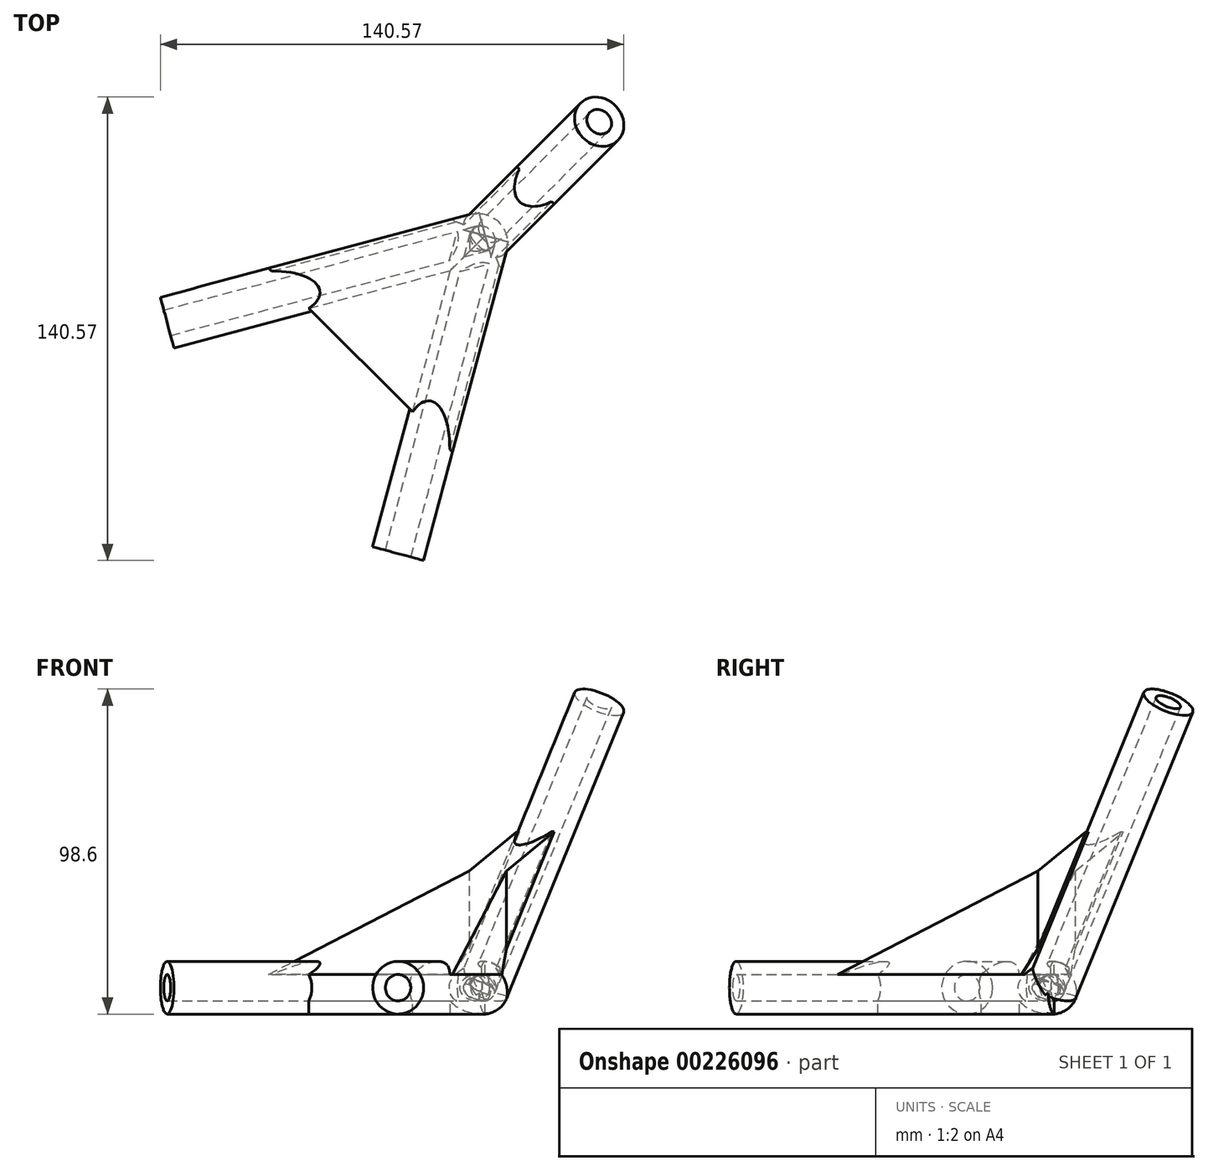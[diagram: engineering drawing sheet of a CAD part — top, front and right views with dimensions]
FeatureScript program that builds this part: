
annotation { "Feature Type Name" : "Feature", "Feature Type Description" : "" }
export const myFeature = defineFeature(function(context is Context, id is Id, definition is map)
    precondition{}
    {
        {
            var Q0;
            Q0=qCreatedBy(makeId("Right.planeOp"),FACE);
            var Q1;
            Q1=qCreatedBy(makeId("Front.planeOp"),FACE);
            cPlane(context, id + "F0", {"entities" : qUnion([Q0, Q1]), "cplaneType" : CPlaneType.MID_PLANE, "offset" : 25.4 * mm, "flipAlignment" : true, "width" : 152.4 * mm, "height" : 152.4 * mm});
        }
        {
            var Q0;
            Q0=qCreatedBy(id+"F0.planeOp",FACE);
            var sketch = newSketch(context, id + "F1", { "sketchPlane" : qUnion([Q0])});
            skLineSegment(sketch, "E0", {"start": v(0, 0) * mm, "end": v(47.64, 82.52) * mm, "construction": true});
            skLineSegment(sketch, "E1", {"start": v(-3.46, 2) * mm, "end": v(46.54, 88.6) * mm});
            skLineSegment(sketch, "E2", {"start": v(46.54, 88.6) * mm, "end": v(43.07, 90.6) * mm});
            skLineSegment(sketch, "E3", {"start": v(43.07, 90.6) * mm, "end": v(-6.93, 4) * mm});
            skLineSegment(sketch, "E4", {"start": v(-6.93, 4) * mm, "end": v(-3.46, 2) * mm});
            skLineSegment(sketch, "E5", {"start": v(0, 0) * mm, "end": v(-3.46, 2) * mm, "construction": true});
            skSolve(sketch);
        }
        {
            var Q0;
            Q0=makeQuery(id+"F1.imprint","IMPRINT",FACE,{"disambiguationData":[TD([[makeQuery(id+"F1.imprint","IMPRINT",EDGE,{"derivedFrom":sQuery(id+"F1.wireOp",EDGE,"E1")}),1.0]])]});
            var Q1;
            Q1=sQuery(id+"F1.wireOp",EDGE,"E0");
            revolve(context, id + "F2", {"entities" : qUnion([Q0]), "axis" : qUnion([Q1]), "revolveType" : RevolveType.FULL});
        }
        {
            var Q0;
            Q0=qCreatedBy(makeId("Top.planeOp"),FACE);
            var sketch = newSketch(context, id + "F3", { "sketchPlane" : qUnion([Q0])});
            skLineSegment(sketch, "E6", {"start": v(0, 0) * mm, "end": v(-27.33, -7.32) * mm, "construction": true});
            skLineSegment(sketch, "E7", {"start": v(1.97, -3.61) * mm, "end": v(-94.62, -29.5) * mm});
            skLineSegment(sketch, "E8", {"start": v(-94.62, -29.5) * mm, "end": v(-93.59, -33.36) * mm});
            skLineSegment(sketch, "E9", {"start": v(-93.59, -33.36) * mm, "end": v(3, -7.48) * mm});
            skLineSegment(sketch, "E10", {"start": v(3, -7.48) * mm, "end": v(1.97, -3.61) * mm});
            skLineSegment(sketch, "E11", {"start": v(0, 0) * mm, "end": v(1.97, -3.61) * mm, "construction": true});
            skSolve(sketch);
        }
        {
            var Q0;
            Q0 = qSketchRegion(id + "F3", true);
            var Q1;
            Q1=sQuery(id+"F3.wireOp",EDGE,"E6");
            revolve(context, id + "F4", {"operationType" : NewBodyOperationType.ADD, "entities" : qUnion([Q0]), "axis" : qUnion([Q1]), "revolveType" : RevolveType.FULL});
        }
        {
            var Q0;
            Q0=makeQuery(id+"F2.opRevolve","SWEPT_BODY",BODY,{"disambiguationData":[OSD([sQuery(id+"F1.wireOp",EDGE,"E1"),sQuery(id+"F1.wireOp",EDGE,"E2"),sQuery(id+"F1.wireOp",EDGE,"E3"),sQuery(id+"F1.wireOp",EDGE,"E4")])]});
            var Q1;
            Q1=qCreatedBy(id+"F0.planeOp",FACE);
            mirror(context, id + "F5", {"operationType" : NewBodyOperationType.ADD, "entities" : qUnion([Q0]), "mirrorPlane" : qUnion([Q1])});
        }
        {
            var Q0;
            Q0=qCreatedBy(id+"F0.planeOp",FACE);
            var sketch = newSketch(context, id + "F6", { "sketchPlane" : qUnion([Q0])});
            skLineSegment(sketch, "E12", {"start": v(-6.93, -4) * mm, "end": v(-85.77, -4) * mm});
            skLineSegment(sketch, "E13", {"start": v(-52.3, 4) * mm, "end": v(-6.93, 4) * mm, "construction": true});
            skLineSegment(sketch, "E14", {"start": v(-0.9, 6.43) * mm, "end": v(22.7, 47.3) * mm, "construction": true});
            skLineSegment(sketch, "E15", {"start": v(45.77, 71.27) * mm, "end": v(2.46, -3.73) * mm});
            skLineSegment(sketch, "E16", {"start": v(-52.3, 4) * mm, "end": v(22.7, 47.3) * mm});
            skPoint(sketch, "E17", {"position": v(-29.62, 4) * mm});
            skLineSegment(sketch, "E18", {"start": v(-52.3, 4) * mm, "end": v(-2.3, 4) * mm});
            skLineSegment(sketch, "E19", {"start": v(-2.3, 4) * mm, "end": v(22.7, 47.3) * mm});
            skSolve(sketch);
        }
        {
            var Q0;
            Q0 = qSketchRegion(id + "F6", true);
            var Q1;
            {var subQ0=makeQuery(id+"F4.opRevolve","SWEPT_FACE",FACE,{"disambiguationData":[OSD([sQuery(id+"F3.wireOp",EDGE,"E10")])]});var subQ1=makeQuery(id+"F4.opRevolve","SWEPT_FACE",FACE,{"disambiguationData":[OSD([sQuery(id+"F3.wireOp",EDGE,"E9")])]});var subQ2=makeQuery(id+"F2.opRevolve","SWEPT_FACE",FACE,{"disambiguationData":[OSD([sQuery(id+"F1.wireOp",EDGE,"E3")])]});var subQ3=makeQuery(id+"F5.opPattern","COPY",FACE,{"derivedFrom":subQ1,"instanceName":"1"});Q1=makeQuery(id+"F5.boolean.opBoolean","SPLIT",FACE,{"disambiguationData":[TD([subQ2,subQ1,subQ0,makeQuery(id+"F5.opPattern","COPY",FACE,{"derivedFrom":makeQuery(id+"F4.opRevolve","SWEPT_FACE",FACE,{"disambiguationData":[OSD([sQuery(id+"F3.wireOp",EDGE,"E8")])]}),"instanceName":"1"}),subQ3,makeQuery(id+"F5.opPattern","COPY",FACE,{"derivedFrom":makeQuery(id+"F4.boolean.opBoolean","SPLIT",FACE,{"disambiguationData":[TD([subQ2])],"derivedFrom":subQ0}),"instanceName":"1"})])],"derivedFrom":subQ3});}
            extrude(context, id + "F7", {"entities" : qUnion([Q0]), "operationType" : NewBodyOperationType.ADD, "endBound" : BoundingType.SYMMETRIC, "endBoundEntityFace" : qUnion([Q1]), "depth" : 86 * mm});
        }
        {
            var Q0;
            {var subQ0=sQuery(id+"F6.wireOp",EDGE,"E16");var subQ1=sQuery(id+"F6.wireOp",EDGE,"E19");var subQ2=sQuery(id+"F6.wireOp",EDGE,"E18");Q0=makeQuery(id+"F7.boolean.opBoolean","SPLIT",FACE,{"disambiguationData":[TD([makeQuery(id+"F4.opRevolve","SWEPT_FACE",FACE,{"disambiguationData":[OSD([sQuery(id+"F3.wireOp",EDGE,"E9")])]}),makeQuery(id+"F7.opExtrude","SWEPT_FACE",FACE,{"disambiguationData":[OSD([subQ0])]}),makeQuery(id+"F7.opExtrude","CAP_FACE",FACE,{"disambiguationData":[OSD([subQ0,subQ2,subQ1])],"isStart":true}),makeQuery(id+"F7.opExtrude","SWEPT_FACE",FACE,{"disambiguationData":[OSD([subQ1])]})])],"derivedFrom":makeQuery(id+"F7.opExtrude","SWEPT_FACE",FACE,{"disambiguationData":[OSD([subQ2])]})});}
            var sketch = newSketch(context, id + "F8", { "sketchPlane" : qUnion([Q0])});
            skLineSegment(sketch, "E20", {"start": v(-11.31, 11.31) * mm, "end": v(-33.36, 93.59) * mm});
            skLineSegment(sketch, "E21", {"start": v(-17.9, 97.73) * mm, "end": v(7.22, 3.98) * mm});
            skLineSegment(sketch, "E22", {"start": v(-3.98, -7.22) * mm, "end": v(-97.73, 17.9) * mm});
            skLineSegment(sketch, "E23", {"start": v(-93.59, 33.36) * mm, "end": v(-11.31, 11.31) * mm});
            skLineSegment(sketch, "E24", {"start": v(7.06, 4.26) * mm, "end": v(66.9, -55.58) * mm});
            skLineSegment(sketch, "E25", {"start": v(55.58, -66.9) * mm, "end": v(-4.26, -7.06) * mm});
            skLineSegment(sketch, "E26", {"start": v(-17.9, 97.73) * mm, "end": v(122.81, 97.73) * mm});
            skLineSegment(sketch, "E27", {"start": v(122.81, 97.73) * mm, "end": v(96.63, -40.84) * mm});
            skLineSegment(sketch, "E28", {"start": v(96.63, -40.84) * mm, "end": v(66.9, -55.58) * mm});
            skLineSegment(sketch, "E29", {"start": v(-97.73, 17.9) * mm, "end": v(-112.5, -12.53) * mm});
            skLineSegment(sketch, "E30", {"start": v(-112.5, -12.53) * mm, "end": v(-65.29, -107.8) * mm});
            skLineSegment(sketch, "E31", {"start": v(-65.29, -107.8) * mm, "end": v(53.1, -129.43) * mm});
            skLineSegment(sketch, "E32", {"start": v(53.1, -129.43) * mm, "end": v(55.58, -66.9) * mm});
            skLineSegment(sketch, "E33.0", {"start": v(46.45, 14.36) * mm, "end": v(20.94, -11.15) * mm});
            skPoint(sketch, "E34.0", {"position": v(-8.28, 65.7) * mm});
            skLineSegment(sketch, "E35.0", {"start": v(-6.58, 67.4) * mm, "end": v(-9.98, 64) * mm});
            skLineSegment(sketch, "E36", {"start": v(-9.1, 64.88) * mm, "end": v(21.7, -10.39) * mm});
            skLineSegment(sketch, "E37.0", {"start": v(11.15, -20.94) * mm, "end": v(-14.36, -46.45) * mm});
            skLineSegment(sketch, "E38.0", {"start": v(-64, 9.98) * mm, "end": v(-67.4, 6.58) * mm});
            skLineSegment(sketch, "E39", {"start": v(-64.88, 9.1) * mm, "end": v(10.39, -21.7) * mm});
            skSolve(sketch);
        }
        {
            var Q0;
            Q0 = qSketchRegion(id + "F8", true);
            extrude(context, id + "F9", {"entities" : qUnion([Q0]), "operationType" : NewBodyOperationType.REMOVE, "endBound" : BoundingType.THROUGH_ALL, "oppositeDirection" : true, "depth" : 25 * mm});
        }
        {
            var Q0;
            {var subQ0=makeQuery(id+"F4.opRevolve","SWEPT_FACE",FACE,{"disambiguationData":[OSD([sQuery(id+"F3.wireOp",EDGE,"E9")])]});Q0=makeQuery(id+"F7.boolean.opBoolean","SPLIT",FACE,{"disambiguationData":[TD([subQ0,makeQuery(id+"F5.opPattern","COPY",FACE,{"derivedFrom":makeQuery(id+"F4.boolean.opBoolean","SPLIT",FACE,{"disambiguationData":[TD([makeQuery(id+"F2.opRevolve","SWEPT_FACE",FACE,{"disambiguationData":[OSD([sQuery(id+"F1.wireOp",EDGE,"E3")])]})])],"derivedFrom":subQ0}),"instanceName":"1"}),makeQuery(id+"F7.opExtrude","SWEPT_FACE",FACE,{"disambiguationData":[OSD([sQuery(id+"F6.wireOp",EDGE,"E16")])]})])],"derivedFrom":makeQuery(id+"F7.opExtrude","SWEPT_FACE",FACE,{"disambiguationData":[OSD([sQuery(id+"F6.wireOp",EDGE,"E18")])]})});}
            var sketch = newSketch(context, id + "F10", { "sketchPlane" : qUnion([Q0])});
            skLineSegment(sketch, "E40.0.0", {"start": v(-21.29, 52.69) * mm, "end": v(-52.69, 21.29) * mm});
            skLineSegment(sketch, "E40.0.1", {"start": v(-52.69, 21.29) * mm, "end": v(-9.8, 9.8) * mm});
            skLineSegment(sketch, "E40.0.2", {"start": v(-9.8, 9.8) * mm, "end": v(-21.29, 52.69) * mm});
            skSolve(sketch);
        }
        {
            var Q0;
            Q0 = qSketchRegion(id + "F10", true);
            extrude(context, id + "F11", {"entities" : qUnion([Q0]), "operationType" : NewBodyOperationType.ADD, "depth" : 12 * mm});
        }
    });
